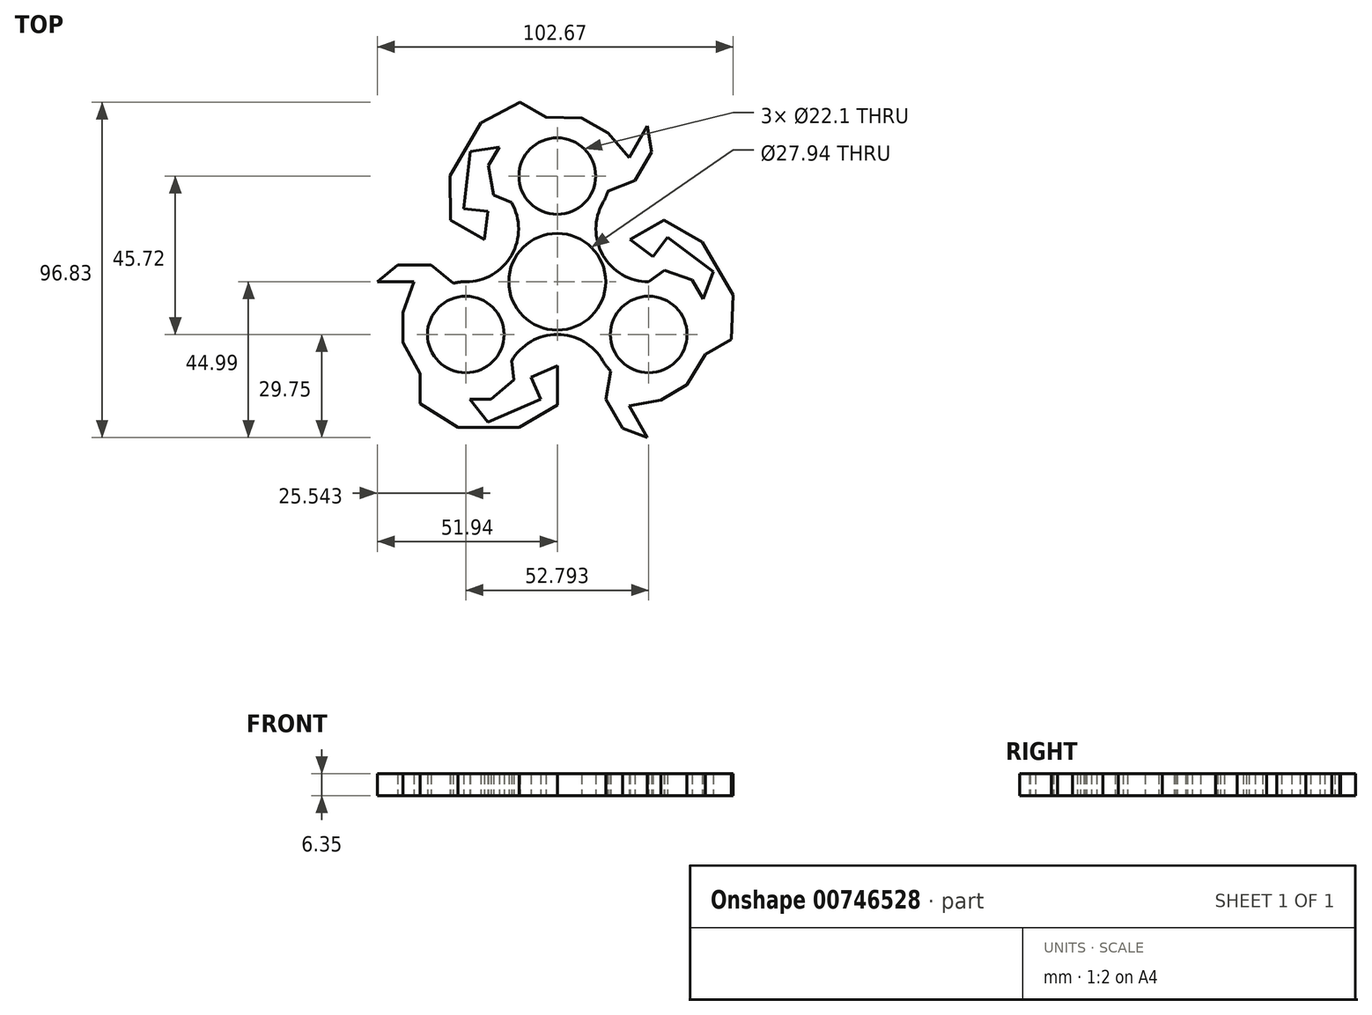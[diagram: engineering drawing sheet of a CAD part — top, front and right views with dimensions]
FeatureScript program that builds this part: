
annotation { "Feature Type Name" : "Feature", "Feature Type Description" : "" }
export const myFeature = defineFeature(function(context is Context, id is Id, definition is map)
    precondition{}
    {
        {
            var Q0;
            Q0=qCreatedBy(makeId("Top.planeOp"),FACE);
            var sketch = newSketch(context, id + "F0", { "sketchPlane" : qUnion([Q0])});
            skCircle(sketch, "E0", {"center": v(0, 0) * mm, "radius": 11.05 * mm});
            skCircle(sketch, "E1", {"center": v(0, 0) * mm, "radius": 13.97 * mm});
            skCircle(sketch, "E2", {"center": v(0, 30.48) * mm, "radius": 11.05 * mm});
            skArc(sketch, "E3", {"start": v(13.2, 22.86) * mm, "mid": v(14, 24.48) * mm, "end": v(14.62, 26.19) * mm});
            skCircle(sketch, "E4.1.0", {"center": v(-26.4, -15.24) * mm, "radius": 11.05 * mm});
            skArc(sketch, "E4.1.1", {"start": v(-26.4, 0) * mm, "mid": v(-28.2, -0.1) * mm, "end": v(-29.99, -0.43) * mm});
            skCircle(sketch, "E4.2.0", {"center": v(26.4, -15.24) * mm, "radius": 11.05 * mm});
            skArc(sketch, "E4.2.1", {"start": v(13.2, -22.86) * mm, "mid": v(14.2, -24.37) * mm, "end": v(15.37, -25.76) * mm});
            skArc(sketch, "E5", {"start": v(-26.4, 0) * mm, "mid": v(-13.2, 7.62) * mm, "end": v(-13.2, 22.86) * mm});
            skArc(sketch, "E6.1.0", {"start": v(13.2, -22.86) * mm, "mid": v(0, -15.24) * mm, "end": v(-13.2, -22.86) * mm});
            skArc(sketch, "E6.2.0", {"start": v(13.2, 22.86) * mm, "mid": v(13.2, 7.62) * mm, "end": v(26.4, 0) * mm});
            skLineSegment(sketch, "E7", {"start": v(-12.56, -28.38) * mm, "end": v(-19.07, -33.96) * mm});
            skLineSegment(sketch, "E8", {"start": v(-25.27, -33.96) * mm, "end": v(-20, -40.47) * mm});
            skLineSegment(sketch, "E9", {"start": v(-20, -40.47) * mm, "end": v(-4.8, -33.96) * mm});
            skLineSegment(sketch, "E10", {"start": v(-4.8, -33.96) * mm, "end": v(-7.57, -27.52) * mm});
            skLineSegment(sketch, "E11", {"start": v(-7.57, -27.52) * mm, "end": v(0, -24.28) * mm});
            skLineSegment(sketch, "E12", {"start": v(0, -24.28) * mm, "end": v(0, -35.5) * mm});
            skLineSegment(sketch, "E13", {"start": v(0, -35.5) * mm, "end": v(-11, -42.02) * mm});
            skLineSegment(sketch, "E14", {"start": v(-11, -42.02) * mm, "end": v(-28.69, -42.02) * mm});
            skLineSegment(sketch, "E15", {"start": v(-28.69, -42.02) * mm, "end": v(-39.54, -35.2) * mm});
            skLineSegment(sketch, "E16", {"start": v(-39.54, -35.2) * mm, "end": v(-39.54, -26.51) * mm});
            skLineSegment(sketch, "E17", {"start": v(-39.54, -26.51) * mm, "end": v(-44.5, -17.52) * mm});
            skLineSegment(sketch, "E18", {"start": v(-44.5, -17.52) * mm, "end": v(-44.5, -8.84) * mm});
            skLineSegment(sketch, "E19", {"start": v(-44.5, -8.84) * mm, "end": v(-41.4, 0) * mm});
            skLineSegment(sketch, "E20", {"start": v(-41.4, 0) * mm, "end": v(-51.94, 0) * mm});
            skLineSegment(sketch, "E21", {"start": v(-51.94, 0) * mm, "end": v(-46.05, 4.8) * mm});
            skLineSegment(sketch, "E22", {"start": v(-46.05, 4.8) * mm, "end": v(-36.44, 4.8) * mm});
            skLineSegment(sketch, "E23", {"start": v(-36.44, 4.8) * mm, "end": v(-29.99, -0.43) * mm});
            skLineSegment(sketch, "E24", {"start": v(-12.56, -28.38) * mm, "end": v(-13.2, -22.86) * mm});
            skLineSegment(sketch, "E25", {"start": v(-25.27, -33.96) * mm, "end": v(-19.07, -33.96) * mm});
            skLineSegment(sketch, "E26.1.0", {"start": v(14.06, -33.96) * mm, "end": v(15.37, -25.76) * mm});
            skLineSegment(sketch, "E26.1.1", {"start": v(18.86, -42.29) * mm, "end": v(14.06, -33.96) * mm});
            skLineSegment(sketch, "E26.1.2", {"start": v(25.97, -44.99) * mm, "end": v(18.86, -42.29) * mm});
            skLineSegment(sketch, "E26.1.3", {"start": v(20.7, -35.85) * mm, "end": v(25.97, -44.99) * mm});
            skLineSegment(sketch, "E26.1.4", {"start": v(29.9, -34.12) * mm, "end": v(20.7, -35.85) * mm});
            skLineSegment(sketch, "E26.1.5", {"start": v(37.42, -29.78) * mm, "end": v(29.9, -34.12) * mm});
            skLineSegment(sketch, "E26.1.6", {"start": v(42.73, -20.99) * mm, "end": v(37.42, -29.78) * mm});
            skLineSegment(sketch, "E26.1.7", {"start": v(50.25, -16.64) * mm, "end": v(42.73, -20.99) * mm});
            skLineSegment(sketch, "E26.1.8", {"start": v(50.73, -3.83) * mm, "end": v(50.25, -16.64) * mm});
            skLineSegment(sketch, "E26.1.9", {"start": v(41.9, 11.48) * mm, "end": v(50.73, -3.83) * mm});
            skLineSegment(sketch, "E26.1.10", {"start": v(30.75, 17.75) * mm, "end": v(41.9, 11.48) * mm});
            skLineSegment(sketch, "E26.1.11", {"start": v(21.03, 12.14) * mm, "end": v(30.75, 17.75) * mm});
            skLineSegment(sketch, "E26.1.12", {"start": v(27.62, 7.2) * mm, "end": v(21.03, 12.14) * mm});
            skLineSegment(sketch, "E26.1.13", {"start": v(31.81, 12.82) * mm, "end": v(27.62, 7.2) * mm});
            skLineSegment(sketch, "E26.1.14", {"start": v(45.05, 2.91) * mm, "end": v(31.81, 12.82) * mm});
            skLineSegment(sketch, "E26.1.15", {"start": v(42.05, -4.9) * mm, "end": v(45.05, 2.91) * mm});
            skLineSegment(sketch, "E26.1.16", {"start": v(42.05, -4.9) * mm, "end": v(38.94, 0.46) * mm});
            skLineSegment(sketch, "E26.1.17", {"start": v(30.85, 3.31) * mm, "end": v(38.94, 0.46) * mm});
            skLineSegment(sketch, "E26.1.18", {"start": v(30.85, 3.31) * mm, "end": v(26.4, 0) * mm});
            skLineSegment(sketch, "E26.2.0", {"start": v(22.38, 29.15) * mm, "end": v(14.62, 26.19) * mm});
            skLineSegment(sketch, "E26.2.1", {"start": v(27.19, 37.48) * mm, "end": v(22.38, 29.15) * mm});
            skLineSegment(sketch, "E26.2.2", {"start": v(25.97, 44.99) * mm, "end": v(27.19, 37.48) * mm});
            skLineSegment(sketch, "E26.2.3", {"start": v(20.7, 35.85) * mm, "end": v(25.97, 44.99) * mm});
            skLineSegment(sketch, "E26.2.4", {"start": v(14.6, 42.96) * mm, "end": v(20.7, 35.85) * mm});
            skLineSegment(sketch, "E26.2.5", {"start": v(7.08, 47.3) * mm, "end": v(14.6, 42.96) * mm});
            skLineSegment(sketch, "E26.2.6", {"start": v(-3.2, 47.5) * mm, "end": v(7.08, 47.3) * mm});
            skLineSegment(sketch, "E26.2.7", {"start": v(-10.71, 51.84) * mm, "end": v(-3.2, 47.5) * mm});
            skLineSegment(sketch, "E26.2.8", {"start": v(-22.05, 45.85) * mm, "end": v(-10.71, 51.84) * mm});
            skLineSegment(sketch, "E26.2.9", {"start": v(-30.89, 30.54) * mm, "end": v(-22.05, 45.85) * mm});
            skLineSegment(sketch, "E26.2.10", {"start": v(-30.75, 17.75) * mm, "end": v(-30.89, 30.54) * mm});
            skLineSegment(sketch, "E26.2.11", {"start": v(-21.03, 12.14) * mm, "end": v(-30.75, 17.75) * mm});
            skLineSegment(sketch, "E26.2.12", {"start": v(-20.05, 20.31) * mm, "end": v(-21.03, 12.14) * mm});
            skLineSegment(sketch, "E26.2.13", {"start": v(-27, 21.14) * mm, "end": v(-20.05, 20.31) * mm});
            skLineSegment(sketch, "E26.2.14", {"start": v(-25.05, 37.56) * mm, "end": v(-27, 21.14) * mm});
            skLineSegment(sketch, "E26.2.15", {"start": v(-16.77, 38.87) * mm, "end": v(-25.05, 37.56) * mm});
            skLineSegment(sketch, "E26.2.16", {"start": v(-16.77, 38.87) * mm, "end": v(-19.87, 33.5) * mm});
            skLineSegment(sketch, "E26.2.17", {"start": v(-18.3, 25.06) * mm, "end": v(-19.87, 33.5) * mm});
            skLineSegment(sketch, "E26.2.18", {"start": v(-18.3, 25.06) * mm, "end": v(-13.2, 22.86) * mm});
            skSolve(sketch);
        }
        {
            var Q0;
            Q0=qSketchRegion(id+"F0",true);
            extrude(context, id + "F1", {"entities" : qUnion([Q0]), "depth" : 6.35 * mm, "offsetDistance" : 25.4 * mm});
        }
    });
